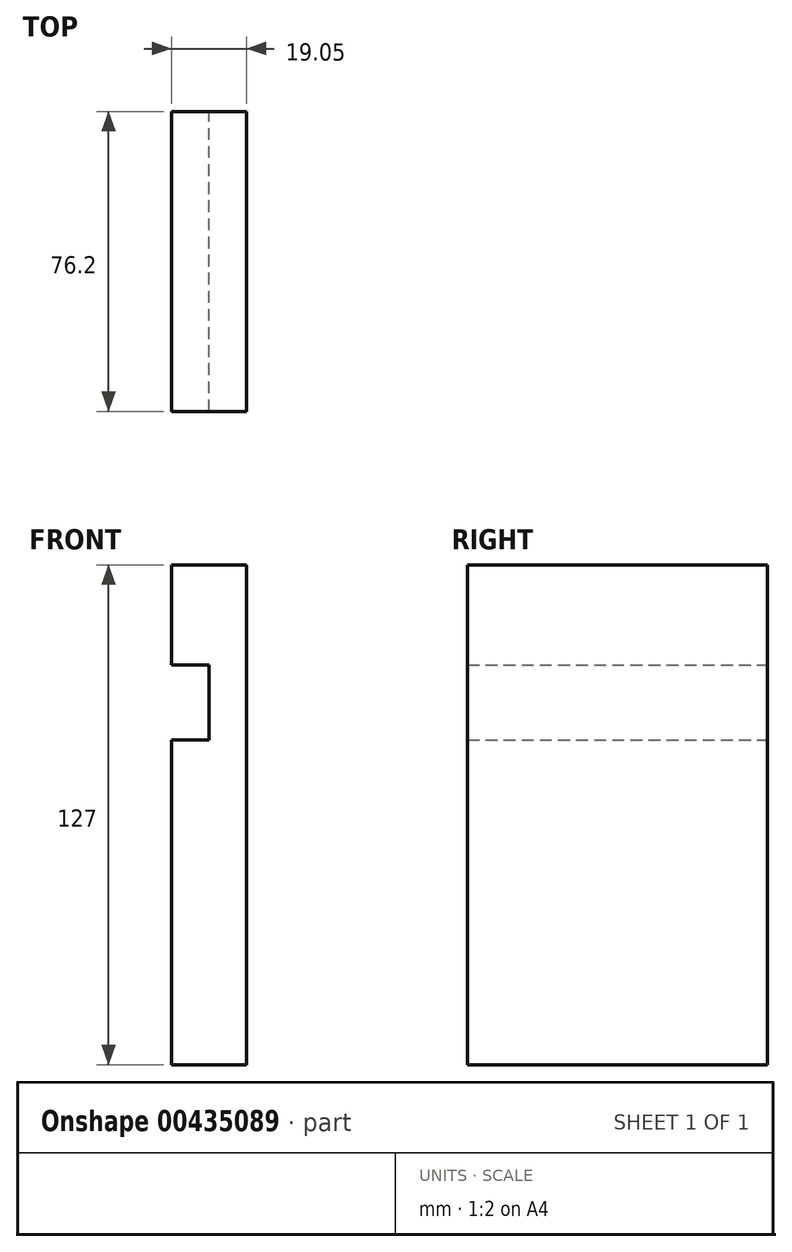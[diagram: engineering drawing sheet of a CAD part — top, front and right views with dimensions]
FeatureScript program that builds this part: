
annotation { "Feature Type Name" : "Feature", "Feature Type Description" : "" }
export const myFeature = defineFeature(function(context is Context, id is Id, definition is map)
    precondition{}
    {
        {
            var Q0;
            Q0=qCreatedBy(makeId("Front.planeOp"),FACE);
            var sketch = newSketch(context, id + "F0", { "sketchPlane" : qUnion([Q0])});
            skLineSegment(sketch, "E0", {"start": v(31.27, -63.59) * mm, "end": v(31.27, 63.41) * mm});
            skLineSegment(sketch, "E1", {"start": v(31.27, 63.41) * mm, "end": v(12.22, 63.41) * mm});
            skLineSegment(sketch, "E2", {"start": v(12.22, 63.41) * mm, "end": v(12.22, 38.01) * mm});
            skLineSegment(sketch, "E3", {"start": v(12.22, 38.01) * mm, "end": v(21.75, 38.01) * mm});
            skLineSegment(sketch, "E4", {"start": v(21.75, 38.01) * mm, "end": v(21.75, 18.96) * mm});
            skLineSegment(sketch, "E5", {"start": v(21.75, 18.96) * mm, "end": v(12.22, 18.96) * mm});
            skLineSegment(sketch, "E6", {"start": v(12.22, 18.96) * mm, "end": v(12.22, -63.59) * mm});
            skLineSegment(sketch, "E7", {"start": v(12.22, -63.59) * mm, "end": v(31.27, -63.59) * mm});
            skSolve(sketch);
        }
        {
            var Q0;
            Q0 = qSketchRegion(id + "F0", true);
            extrude(context, id + "F1", {"entities" : qUnion([Q0]), "depth" : 76.2 * mm});
        }
    });
